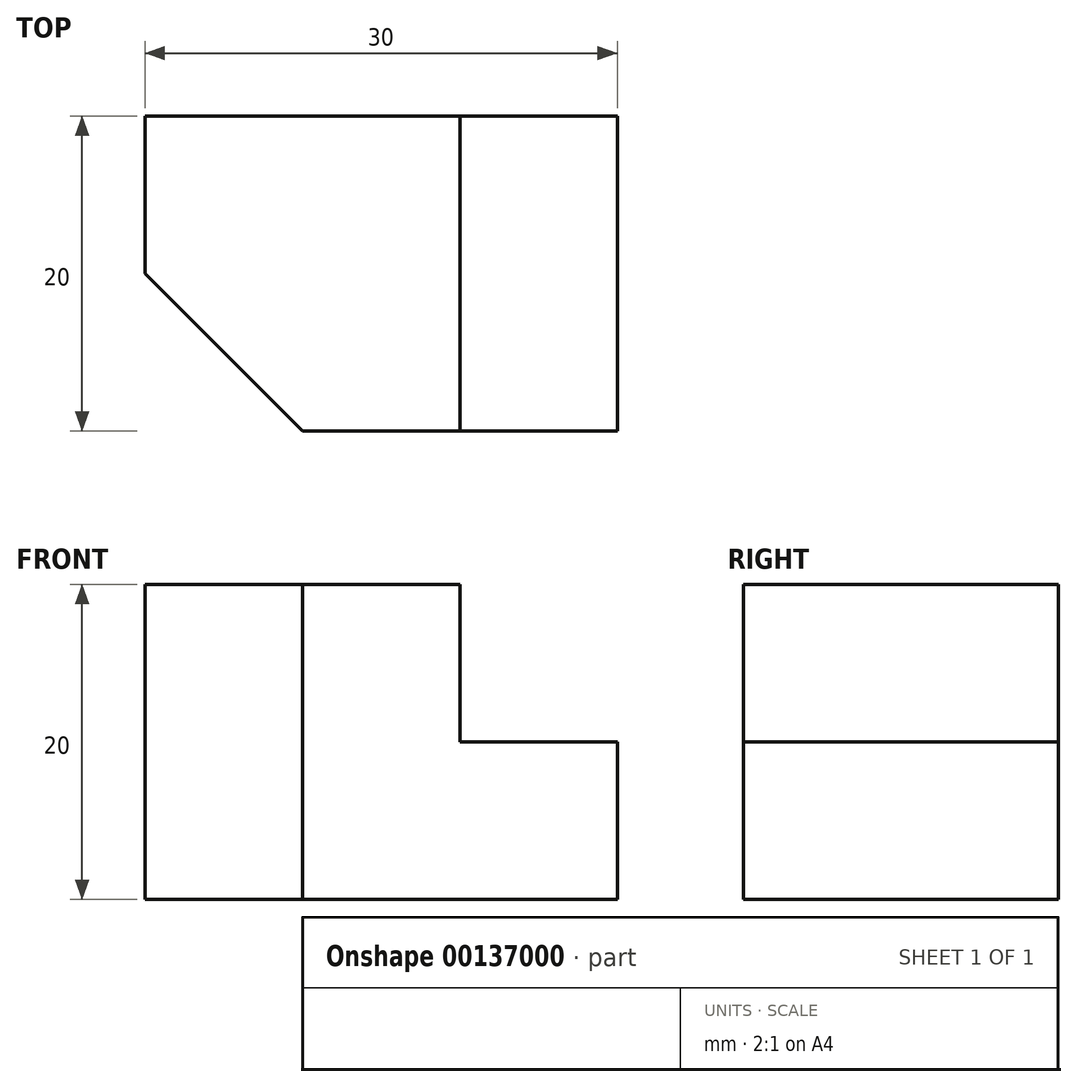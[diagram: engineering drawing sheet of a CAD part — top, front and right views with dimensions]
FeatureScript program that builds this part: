
annotation { "Feature Type Name" : "Feature", "Feature Type Description" : "" }
export const myFeature = defineFeature(function(context is Context, id is Id, definition is map)
    precondition{}
    {
        {
            var Q0;
            Q0=qCreatedBy(makeId("Top.planeOp"),FACE);
            var sketch = newSketch(context, id + "F0", { "sketchPlane" : qUnion([Q0])});
            skLineSegment(sketch, "E0", {"start": v(0, 0) * mm, "end": v(30, 0) * mm});
            skLineSegment(sketch, "E1", {"start": v(30, 0) * mm, "end": v(30, -20) * mm});
            skLineSegment(sketch, "E2", {"start": v(30, -20) * mm, "end": v(10, -20) * mm});
            skLineSegment(sketch, "E3", {"start": v(10, -20) * mm, "end": v(0, -10) * mm});
            skLineSegment(sketch, "E4", {"start": v(0, -10) * mm, "end": v(0, 0) * mm});
            skSolve(sketch);
        }
        {
            var Q0;
            Q0 = qSketchRegion(id + "F0", true);
            extrude(context, id + "F1", {"entities" : qUnion([Q0]), "depth" : 20 * mm});
        }
        {
            var Q0;
            Q0=makeQuery(id+"F1.opExtrude","SWEPT_FACE",FACE,{"disambiguationData":[OSD([sQuery(id+"F0.wireOp",EDGE,"E2")])]});
            var sketch = newSketch(context, id + "F2", { "sketchPlane" : qUnion([Q0])});
            skLineSegment(sketch, "E5.bottom", {"start": v(30, 20) * mm, "end": v(20, 20) * mm});
            skLineSegment(sketch, "E5.top", {"start": v(30, 10) * mm, "end": v(20, 10) * mm});
            skLineSegment(sketch, "E5.left", {"start": v(30, 20) * mm, "end": v(30, 10) * mm});
            skLineSegment(sketch, "E5.right", {"start": v(20, 20) * mm, "end": v(20, 10) * mm});
            skSolve(sketch);
        }
        {
            var Q0;
            Q0 = qSketchRegion(id + "F2", true);
            var Q1;
            Q1=makeQuery(id+"F1.opExtrude","SWEPT_FACE",FACE,{"disambiguationData":[OSD([sQuery(id+"F0.wireOp",EDGE,"E0")])]});
            extrude(context, id + "F3", {"entities" : qUnion([Q0]), "operationType" : NewBodyOperationType.REMOVE, "endBound" : BoundingType.UP_TO_SURFACE, "oppositeDirection" : true, "endBoundEntityFace" : qUnion([Q1]), "depth" : 25 * mm});
        }
    });
